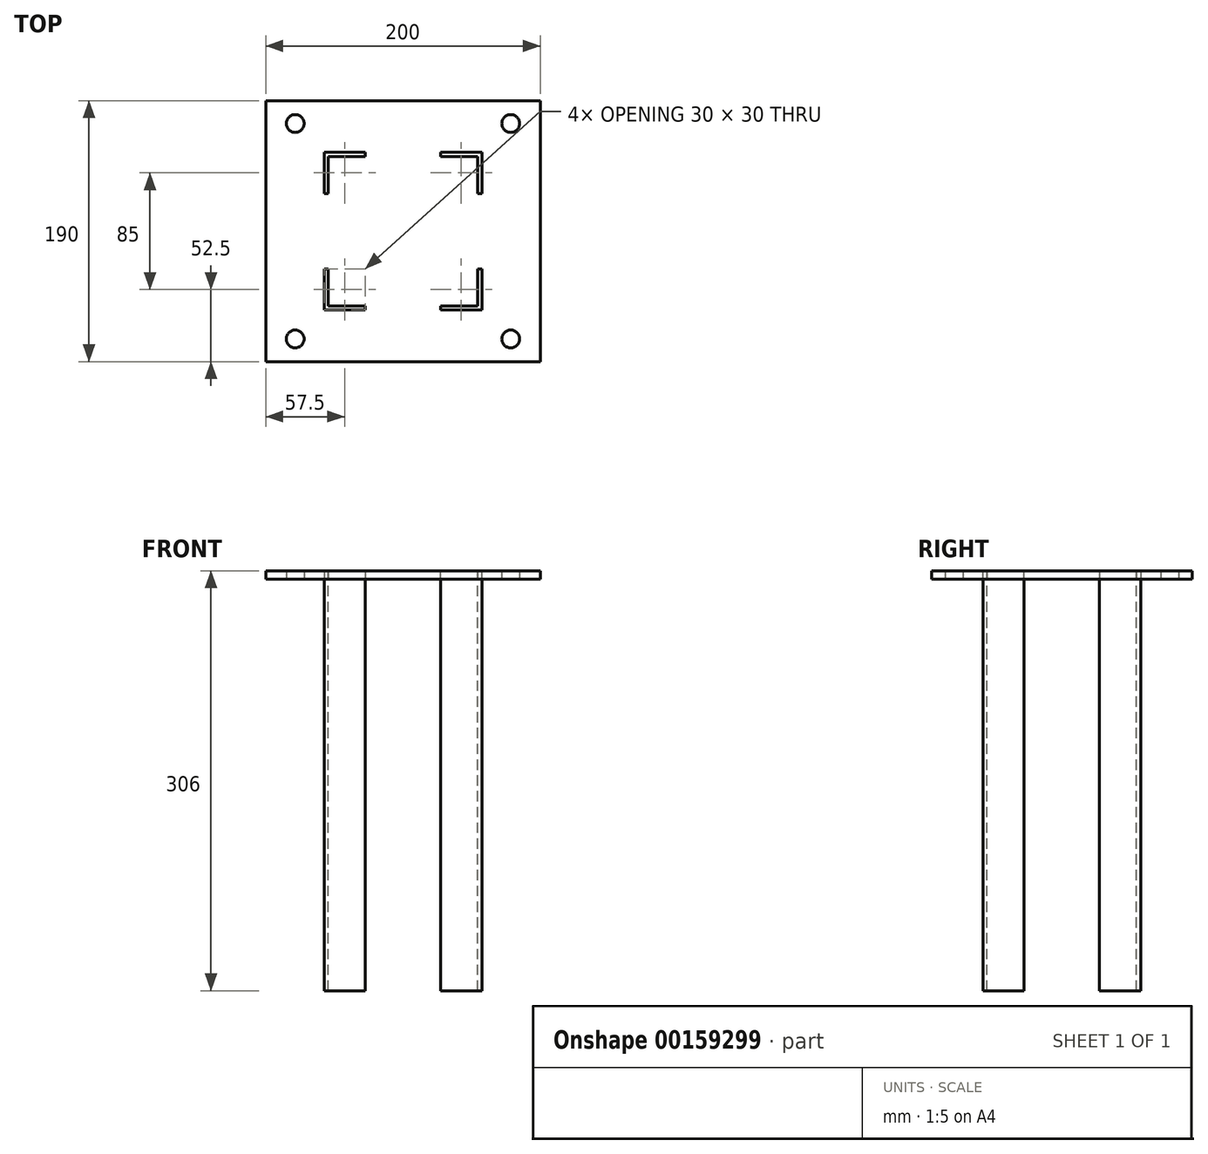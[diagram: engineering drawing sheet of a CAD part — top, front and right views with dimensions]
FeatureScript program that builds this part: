
annotation { "Feature Type Name" : "Feature", "Feature Type Description" : "" }
export const myFeature = defineFeature(function(context is Context, id is Id, definition is map)
    precondition{}
    {
        {
            var Q0;
            Q0=qCreatedBy(makeId("Top.planeOp"),FACE);
            var sketch = newSketch(context, id + "F0", { "sketchPlane" : qUnion([Q0])});
            skLineSegment(sketch, "E0.bottom", {"start": v(100, -95) * mm, "end": v(-100, -95) * mm});
            skLineSegment(sketch, "E0.top", {"start": v(100, 95) * mm, "end": v(-100, 95) * mm});
            skLineSegment(sketch, "E0.left", {"start": v(100, -95) * mm, "end": v(100, 95) * mm});
            skLineSegment(sketch, "E0.right", {"start": v(-100, -95) * mm, "end": v(-100, 95) * mm});
            skPoint(sketch, "E0.middle", {"position": v(0, 0) * mm});
            skCircle(sketch, "E1", {"center": v(-78.5, 78.5) * mm, "radius": 6.5 * mm});
            skCircle(sketch, "E2", {"center": v(78.5, 78.5) * mm, "radius": 6.5 * mm});
            skCircle(sketch, "E3", {"center": v(-78.5, -78.5) * mm, "radius": 6.5 * mm});
            skCircle(sketch, "E4", {"center": v(78.5, -78.5) * mm, "radius": 6.5 * mm});
            skLineSegment(sketch, "E5", {"start": v(-57.5, 57.5) * mm, "end": v(-57.5, 27.5) * mm});
            skLineSegment(sketch, "E6", {"start": v(-57.5, 57.5) * mm, "end": v(-27.5, 57.5) * mm});
            skLineSegment(sketch, "E7", {"start": v(27.5, 57.5) * mm, "end": v(57.5, 57.5) * mm});
            skLineSegment(sketch, "E8", {"start": v(57.5, 57.5) * mm, "end": v(57.5, 27.5) * mm});
            skLineSegment(sketch, "E9", {"start": v(57.5, -27.5) * mm, "end": v(57.5, -57.5) * mm});
            skLineSegment(sketch, "E10", {"start": v(57.5, -57.5) * mm, "end": v(27.5, -57.5) * mm});
            skLineSegment(sketch, "E11", {"start": v(-57.5, -27.5) * mm, "end": v(-57.5, -57.5) * mm});
            skLineSegment(sketch, "E12", {"start": v(-57.5, -57.5) * mm, "end": v(-27.5, -57.5) * mm});
            skLineSegment(sketch, "E13.0", {"start": v(-54.5, -54.5) * mm, "end": v(-27.5, -54.5) * mm});
            skLineSegment(sketch, "E13.1", {"start": v(-54.5, -27.5) * mm, "end": v(-54.5, -54.5) * mm});
            skLineSegment(sketch, "E14", {"start": v(-57.5, -27.5) * mm, "end": v(-54.5, -27.5) * mm});
            skLineSegment(sketch, "E15", {"start": v(-27.5, -54.5) * mm, "end": v(-27.5, -57.5) * mm});
            skPoint(sketch, "E16.start.orphan", {"position": v(57.5, -27.5) * mm});
            skLineSegment(sketch, "E17.0", {"start": v(54.5, -54.5) * mm, "end": v(27.5, -54.5) * mm});
            skLineSegment(sketch, "E17.1", {"start": v(54.5, -27.5) * mm, "end": v(54.5, -54.5) * mm});
            skLineSegment(sketch, "E18.0", {"start": v(54.5, 54.5) * mm, "end": v(54.5, 27.5) * mm});
            skLineSegment(sketch, "E18.1", {"start": v(27.5, 54.5) * mm, "end": v(54.5, 54.5) * mm});
            skLineSegment(sketch, "E19.0", {"start": v(-54.5, 54.5) * mm, "end": v(-27.5, 54.5) * mm});
            skLineSegment(sketch, "E19.1", {"start": v(-54.5, 54.5) * mm, "end": v(-54.5, 27.5) * mm});
            skLineSegment(sketch, "E20", {"start": v(54.5, -27.5) * mm, "end": v(57.5, -27.5) * mm});
            skLineSegment(sketch, "E21", {"start": v(27.5, -54.5) * mm, "end": v(27.5, -57.5) * mm});
            skLineSegment(sketch, "E22", {"start": v(57.5, 27.5) * mm, "end": v(54.5, 27.5) * mm});
            skLineSegment(sketch, "E23", {"start": v(27.5, 57.5) * mm, "end": v(27.5, 54.5) * mm});
            skLineSegment(sketch, "E24", {"start": v(-27.5, 57.5) * mm, "end": v(-27.5, 54.5) * mm});
            skLineSegment(sketch, "E25", {"start": v(-57.5, 27.5) * mm, "end": v(-54.5, 27.5) * mm});
            skPoint(sketch, "E26.orphan", {"position": v(-57.5, 42.5) * mm});
            skPoint(sketch, "E27.start.orphan", {"position": v(-57.5, -42.5) * mm});
            skPoint(sketch, "E28.start.orphan", {"position": v(57.5, -42.5) * mm});
            skSolve(sketch);
        }
        {
            var Q0;
            Q0=makeQuery(id+"F0.imprint","IMPRINT",FACE,{"disambiguationData":[TD([[makeQuery(id+"F0.imprint","IMPRINT",EDGE,{"derivedFrom":sQuery(id+"F0.wireOp",EDGE,"E11")}),-1.0]])]});
            var sketch = newSketch(context, id + "F1", { "sketchPlane" : qUnion([Q0])});
            skSolve(sketch);
        }
        {
            var Q0;
            Q0 = qSketchRegion(id + "F0", true);
            extrude(context, id + "F2", {"entities" : qUnion([Q0]), "depth" : 6 * mm});
        }
        {
            var Q0;
            Q0=makeQuery(id+"F1.imprint","IMPRINT",FACE,{"disambiguationData":[TD([[makeQuery(id+"F1.imprint","IMPRINT",EDGE,{"derivedFrom":makeQuery(id+"F0.imprint","IMPRINT",EDGE,{"derivedFrom":sQuery(id+"F0.wireOp",EDGE,"E11")})}),1.0]])]});
            var Q1;
            Q1=makeQuery(id+"F1.imprint","IMPRINT",FACE,{"disambiguationData":[TD([[makeQuery(id+"F1.imprint","IMPRINT",EDGE,{"derivedFrom":makeQuery(id+"F0.imprint","IMPRINT",EDGE,{"derivedFrom":sQuery(id+"F0.wireOp",EDGE,"E5")})}),1.0]])]});
            var Q2;
            Q2=makeQuery(id+"F1.imprint","IMPRINT",FACE,{"disambiguationData":[TD([[makeQuery(id+"F1.imprint","IMPRINT",EDGE,{"derivedFrom":makeQuery(id+"F0.imprint","IMPRINT",EDGE,{"derivedFrom":sQuery(id+"F0.wireOp",EDGE,"E7")})}),-1.0]])]});
            var Q3;
            Q3=makeQuery(id+"F1.imprint","IMPRINT",FACE,{"disambiguationData":[TD([[makeQuery(id+"F1.imprint","IMPRINT",EDGE,{"derivedFrom":makeQuery(id+"F0.imprint","IMPRINT",EDGE,{"derivedFrom":sQuery(id+"F0.wireOp",EDGE,"E9")})}),-1.0]])]});
            extrude(context, id + "F3", {"entities" : qUnion([Q0, Q1, Q2, Q3]), "oppositeDirection" : true, "depth" : 300 * mm, "hasSecondDirection" : true, "secondDirectionOppositeDirection" : false, "secondDirectionDepth" : 6 * mm});
        }
    });
